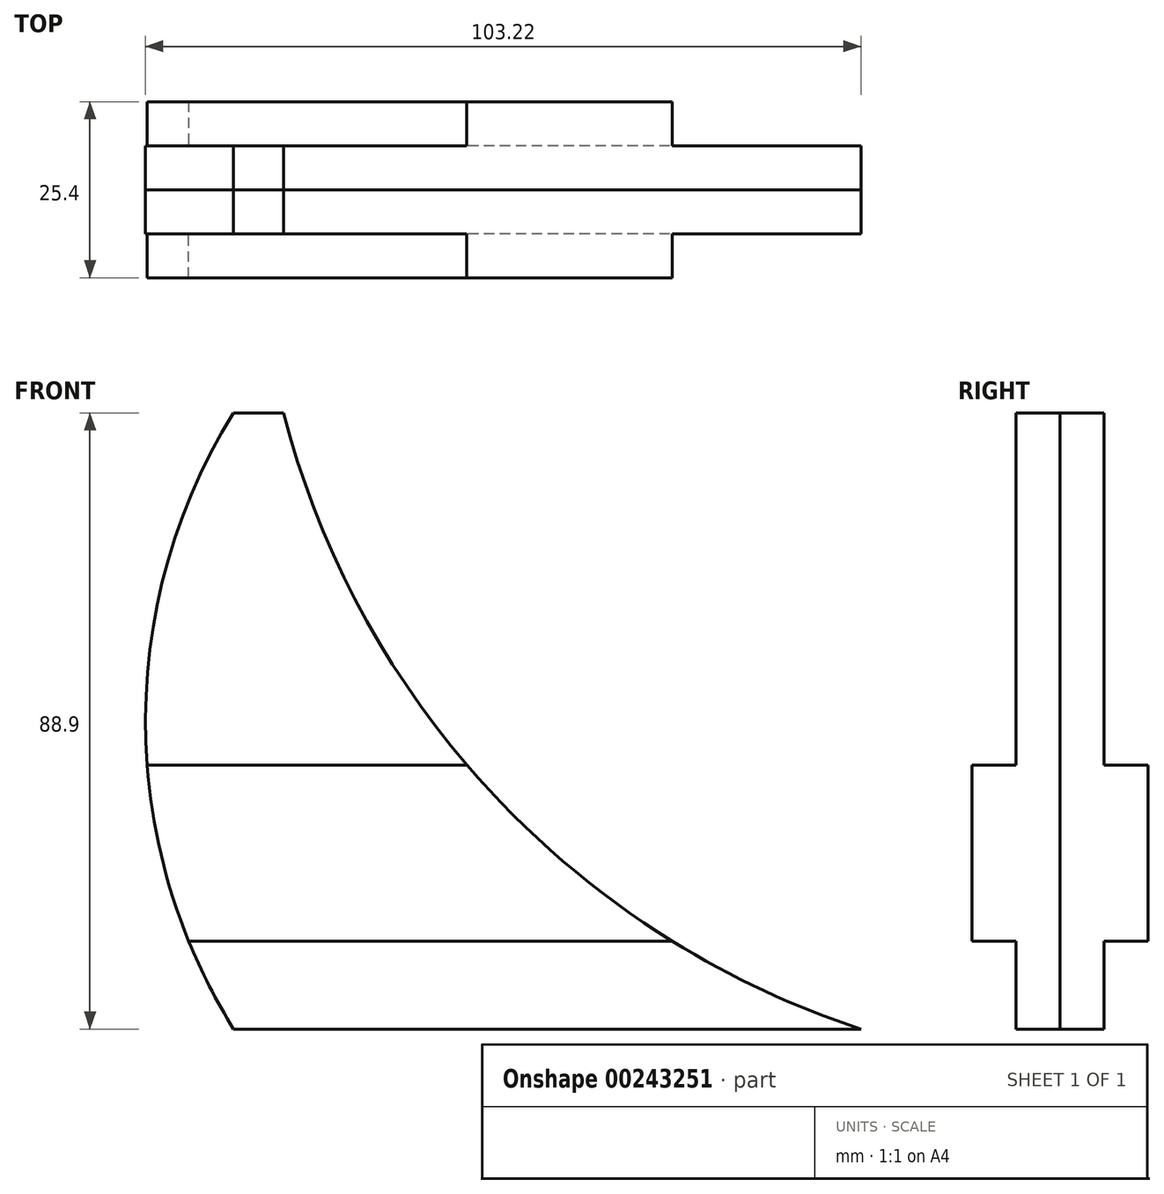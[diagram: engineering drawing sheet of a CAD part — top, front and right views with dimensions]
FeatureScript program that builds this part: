
annotation { "Feature Type Name" : "Feature", "Feature Type Description" : "" }
export const myFeature = defineFeature(function(context is Context, id is Id, definition is map)
    precondition{}
    {
        {
            var Q0;
            Q0=qCreatedBy(makeId("Front.planeOp"),FACE);
            var sketch = newSketch(context, id + "F0", { "sketchPlane" : qUnion([Q0])});
            skLineSegment(sketch, "E0.bottom", {"start": v(0, 0) * mm, "end": v(-104.78, 0) * mm});
            skLineSegment(sketch, "E0.top", {"start": v(0, 88.9) * mm, "end": v(-104.78, 88.9) * mm});
            skLineSegment(sketch, "E0.left", {"start": v(0, 0) * mm, "end": v(0, 88.9) * mm});
            skLineSegment(sketch, "E0.right", {"start": v(-104.78, 0) * mm, "end": v(-104.78, 88.9) * mm});
            skSolve(sketch);
        }
        {
            var Q0;
            Q0=makeQuery(id+"F0.imprint","IMPRINT",FACE,{"disambiguationData":[TD([[makeQuery(id+"F0.imprint","IMPRINT",EDGE,{"derivedFrom":sQuery(id+"F0.wireOp",EDGE,"E0.bottom")}),-1.0]])]});
            extrude(context, id + "F1", {"entities" : qUnion([Q0]), "depth" : 6.35 * mm});
        }
        {
            var Q0;
            Q0=makeQuery(id+"F1.opExtrude","CAP_FACE",FACE,{"disambiguationData":[OSD([sQuery(id+"F0.wireOp",EDGE,"E0.bottom"),sQuery(id+"F0.wireOp",EDGE,"E0.top"),sQuery(id+"F0.wireOp",EDGE,"E0.left"),sQuery(id+"F0.wireOp",EDGE,"E0.right")])],"isStart":true});
            var sketch = newSketch(context, id + "F2", { "sketchPlane" : qUnion([Q0])});
            skLineSegment(sketch, "E1", {"start": v(0, 12.7) * mm, "end": v(104.78, 12.7) * mm});
            skLineSegment(sketch, "E2", {"start": v(0, 38.1) * mm, "end": v(104.78, 38.1) * mm});
            skSolve(sketch);
        }
        {
            var Q0;
            Q0 = qSketchRegion(id + "F2", true);
            var Q1;
            {var subQ0=sQuery(id+"F2.wireOp",EDGE,"E1");Q1=makeQuery(id+"F2.imprint","IMPRINT",FACE,{"disambiguationData":[TD([[makeQuery(id+"F2.imprint","IMPRINT",EDGE,{"derivedFrom":subQ0}),1.0]])]});}
            extrude(context, id + "F3", {"entities" : qUnion([Q0, Q1]), "operationType" : NewBodyOperationType.ADD, "depth" : 6.35 * mm});
        }
        {
            var Q0;
            Q0=makeQuery(id+"F1.opExtrude","CAP_FACE",FACE,{"disambiguationData":[OSD([sQuery(id+"F0.wireOp",EDGE,"E0.bottom"),sQuery(id+"F0.wireOp",EDGE,"E0.top"),sQuery(id+"F0.wireOp",EDGE,"E0.left"),sQuery(id+"F0.wireOp",EDGE,"E0.right")])],"isStart":false});
            var sketch = newSketch(context, id + "F4", { "sketchPlane" : qUnion([Q0])});
            skLineSegment(sketch, "E3", {"start": v(-20.64, 88.9) * mm, "end": v(-20.64, 44.45) * mm});
            skLineSegment(sketch, "E4", {"start": v(-20.64, 44.45) * mm, "end": v(0, 44.45) * mm});
            skCircle(sketch, "E5", {"center": v(-20.64, 44.45) * mm, "radius": 84.14 * mm});
            skSolve(sketch);
        }
        {
            var Q0;
            {var subQ0=sQuery(id+"F4.wireOp",EDGE,"E5");var subQ1=makeQuery(id+"F1.opExtrude","CAP_EDGE",EDGE,{"disambiguationData":[OSD([sQuery(id+"F0.wireOp",EDGE,"E0.right")])],"isStart":false});var subQ2=makeQuery(id+"F4.imprint","INTERSECT",VERTEX,{"derivedFrom":[subQ1,subQ0]});Q0=makeQuery(id+"F4.imprint","IMPRINT",FACE,{"disambiguationData":[TD([[makeQuery(id+"F4.imprint","IMPRINT",EDGE,{"disambiguationData":[TD([[subQ2,-1.0]])],"derivedFrom":subQ0}),-1.0]])]});}
            var Q1;
            {var subQ0=sQuery(id+"F4.wireOp",EDGE,"E5");var subQ1=makeQuery(id+"F1.opExtrude","CAP_EDGE",EDGE,{"disambiguationData":[OSD([sQuery(id+"F0.wireOp",EDGE,"E0.right")])],"isStart":false});var subQ2=makeQuery(id+"F4.imprint","INTERSECT",VERTEX,{"derivedFrom":[subQ1,subQ0]});Q1=makeQuery(id+"F4.imprint","IMPRINT",FACE,{"disambiguationData":[TD([[makeQuery(id+"F4.imprint","IMPRINT",EDGE,{"disambiguationData":[TD([[subQ2,1.0]])],"derivedFrom":subQ0}),-1.0]])]});}
            extrude(context, id + "F5", {"entities" : qUnion([Q0, Q1]), "operationType" : NewBodyOperationType.REMOVE, "oppositeDirection" : true, "depth" : 254 * mm});
        }
        {
            var Q0;
            Q0=makeQuery(id+"F1.opExtrude","CAP_FACE",FACE,{"disambiguationData":[OSD([sQuery(id+"F0.wireOp",EDGE,"E0.bottom"),sQuery(id+"F0.wireOp",EDGE,"E0.top"),sQuery(id+"F0.wireOp",EDGE,"E0.left"),sQuery(id+"F0.wireOp",EDGE,"E0.right")])],"isStart":false});
            var sketch = newSketch(context, id + "F6", { "sketchPlane" : qUnion([Q0])});
            skLineSegment(sketch, "E6", {"start": v(0, 88.9) * mm, "end": v(0, 120.65) * mm});
            skLineSegment(sketch, "E7", {"start": v(0, 120.65) * mm, "end": v(38.1, 120.65) * mm});
            skCircle(sketch, "E8", {"center": v(38.1, 88.9) * mm, "radius": 127 * mm});
            skCircle(sketch, "E9", {"center": v(38.1, 120.65) * mm, "radius": 127 * mm});
            skSolve(sketch);
        }
        {
            var Q0;
            {var subQ5=makeQuery(id+"F1.opExtrude","CAP_EDGE",EDGE,{"disambiguationData":[OSD([sQuery(id+"F0.wireOp",EDGE,"E0.left")])],"isStart":false});Q0=makeQuery(id+"F6.imprint","IMPRINT",FACE,{"disambiguationData":[TD([[makeQuery(id+"F6.imprint","IMPRINT",EDGE,{"derivedFrom":subQ5}),1.0]])]});}
            extrude(context, id + "F7", {"entities" : qUnion([Q0]), "operationType" : NewBodyOperationType.REMOVE, "oppositeDirection" : true, "depth" : 25.4 * mm});
        }
        {
            var Q0;
            Q0=makeQuery(id+"F1.opExtrude","SWEPT_BODY",BODY,{"disambiguationData":[OSD([sQuery(id+"F0.wireOp",EDGE,"E0.bottom"),sQuery(id+"F0.wireOp",EDGE,"E0.top"),sQuery(id+"F0.wireOp",EDGE,"E0.left"),sQuery(id+"F0.wireOp",EDGE,"E0.right")])]});
            var Q1;
            Q1=makeQuery(id+"F1.opExtrude","CAP_FACE",FACE,{"disambiguationData":[OSD([sQuery(id+"F0.wireOp",EDGE,"E0.bottom"),sQuery(id+"F0.wireOp",EDGE,"E0.top"),sQuery(id+"F0.wireOp",EDGE,"E0.left"),sQuery(id+"F0.wireOp",EDGE,"E0.right")])],"isStart":false});
            mirror(context, id + "F8", {"entities" : qUnion([Q0]), "mirrorPlane" : qUnion([Q1])});
        }
    });
